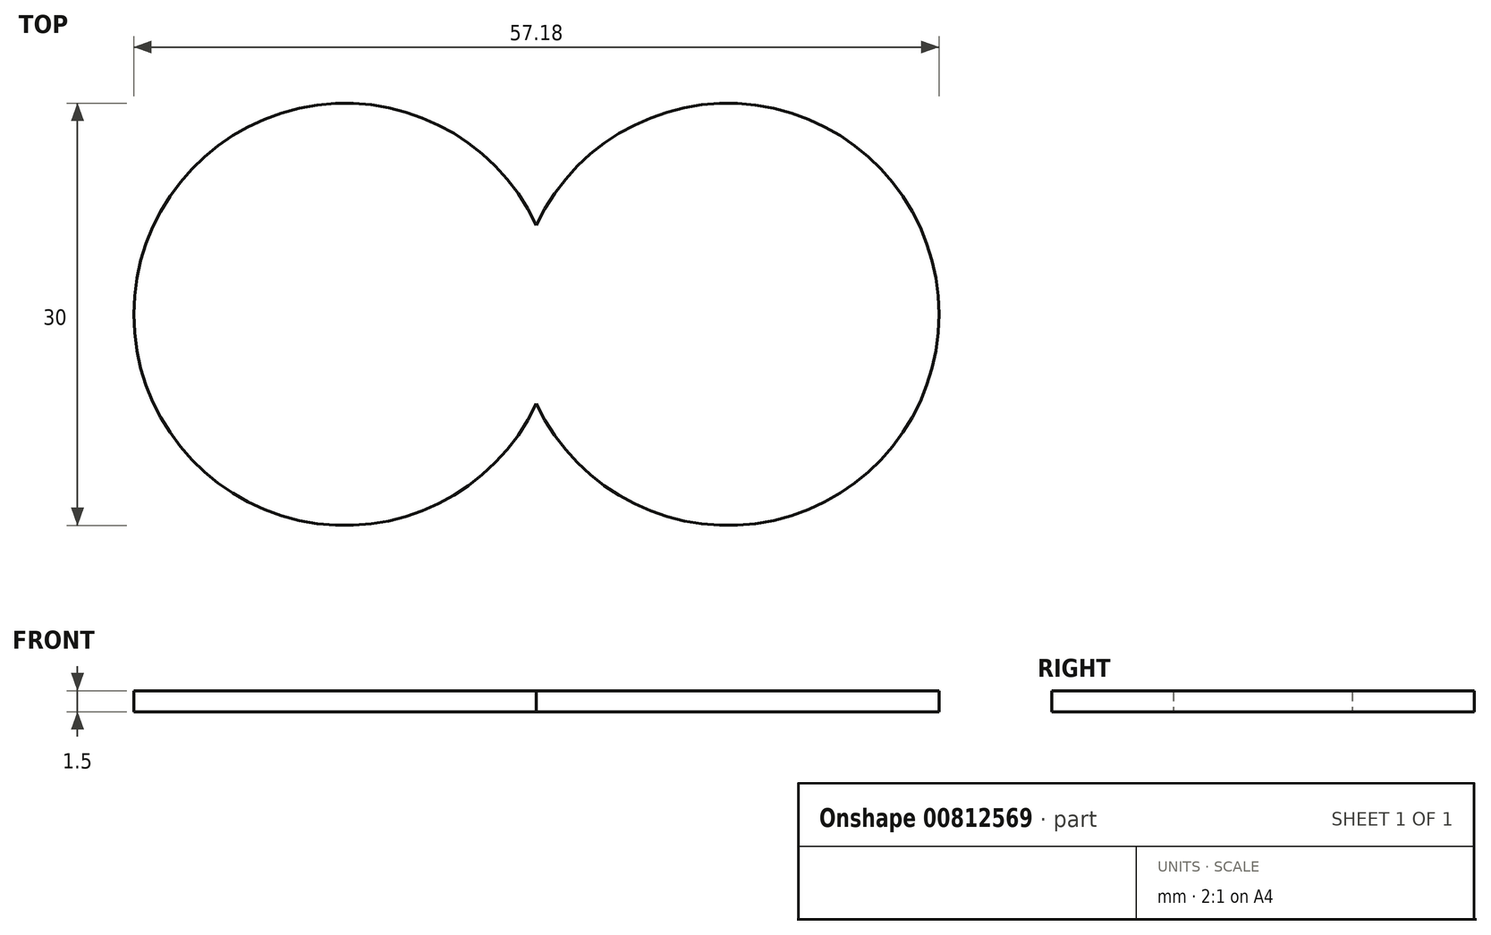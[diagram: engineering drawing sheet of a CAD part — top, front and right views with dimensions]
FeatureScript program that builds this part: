
annotation { "Feature Type Name" : "Feature", "Feature Type Description" : "" }
export const myFeature = defineFeature(function(context is Context, id is Id, definition is map)
    precondition{}
    {
        {
            var Q0;
            Q0=qCreatedBy(makeId("Top.planeOp"),FACE);
            var sketch = newSketch(context, id + "F0", { "sketchPlane" : qUnion([Q0])});
            skCircle(sketch, "E0", {"center": v(-13.6, -32.92) * mm, "radius": 15 * mm});
            skCircle(sketch, "E1.MirrorC", {"center": v(13.6, -32.92) * mm, "radius": 15 * mm});
            skSolve(sketch);
        }
        {
            var Q0;
            {var subQ0=sQuery(id+"F0.wireOp",EDGE,"E1.MirrorC");var subQ1=sQuery(id+"F0.wireOp",EDGE,"E0");var subQ2=makeQuery(id+"F0.imprint","INTERSECT",VERTEX,{"disambiguationData":[OD(0.0)],"derivedFrom":[subQ1,subQ0]});Q0=makeQuery(id+"F0.imprint","IMPRINT",FACE,{"disambiguationData":[TD([[makeQuery(id+"F0.imprint","IMPRINT",EDGE,{"disambiguationData":[TD([[subQ2,1.0]])],"derivedFrom":subQ1}),1.0]])]});}
            var Q1;
            {var subQ0=sQuery(id+"F0.wireOp",EDGE,"E1.MirrorC");var subQ1=sQuery(id+"F0.wireOp",EDGE,"E0");var subQ2=makeQuery(id+"F0.imprint","INTERSECT",VERTEX,{"disambiguationData":[OD(0.0)],"derivedFrom":[subQ1,subQ0]});Q1=makeQuery(id+"F0.imprint","IMPRINT",FACE,{"disambiguationData":[TD([[makeQuery(id+"F0.imprint","IMPRINT",EDGE,{"disambiguationData":[TD([[subQ2,-1.0]])],"derivedFrom":subQ1}),1.0]])]});}
            var Q2;
            {var subQ0=sQuery(id+"F0.wireOp",EDGE,"E1.MirrorC");var subQ1=sQuery(id+"F0.wireOp",EDGE,"E0");var subQ2=makeQuery(id+"F0.imprint","INTERSECT",VERTEX,{"disambiguationData":[OD(0.0)],"derivedFrom":[subQ1,subQ0]});Q2=makeQuery(id+"F0.imprint","IMPRINT",FACE,{"disambiguationData":[TD([[makeQuery(id+"F0.imprint","IMPRINT",EDGE,{"disambiguationData":[TD([[subQ2,-1.0]])],"derivedFrom":subQ1}),-1.0]])]});}
            extrude(context, id + "F1", {"entities" : qUnion([Q0, Q1, Q2]), "depth" : 1.5 * mm, "offsetDistance" : 25 * mm});
        }
    });
